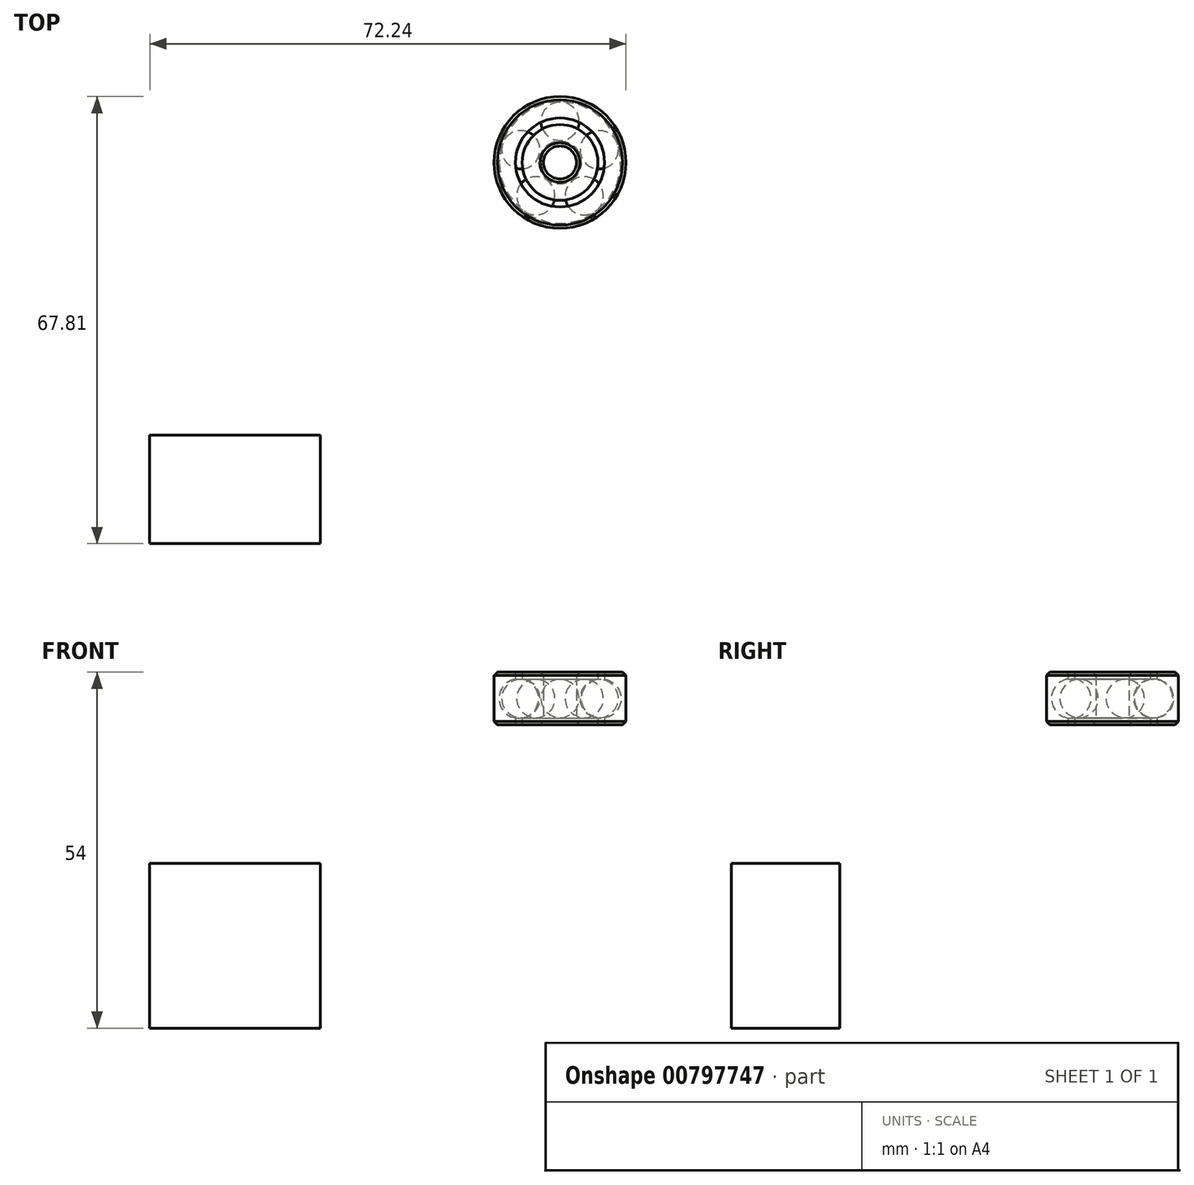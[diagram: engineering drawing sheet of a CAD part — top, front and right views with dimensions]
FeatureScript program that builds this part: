
annotation { "Feature Type Name" : "Feature", "Feature Type Description" : "" }
export const myFeature = defineFeature(function(context is Context, id is Id, definition is map)
    precondition{}
    {
        {
            assignVariable(context, id + "F0", {"name" : "espacio_alto", "anyValue" : 50});
        }
        {
            assignVariable(context, id + "F1", {"name" : "espacio_atras", "anyValue" : 0});
        }
        {
            assignVariable(context, id + "F2", {"name" : "espacio_lateral", "anyValue" : 0});
        }
        {
            var Q0;
            Q0=qCreatedBy(makeId("Right.planeOp"),FACE);
            var sketch = newSketch(context, id + "F3", { "sketchPlane" : qUnion([Q0])});
            skLineSegment(sketch, "E0", {"start": v(0, 0) * mm, "end": v(0, 7.32) * mm, "construction": true});
            skArc(sketch, "E1", {"start": v(6.25, 3) * mm, "mid": v(9.25, 0) * mm, "end": v(6.25, -3) * mm});
            skLineSegment(sketch, "E2", {"start": v(6.25, 3) * mm, "end": v(6.25, -3) * mm});
            skLineSegment(sketch, "E3", {"start": v(6.75, 2.96) * mm, "end": v(6.75, -2.96) * mm});
            skLineSegment(sketch, "E4", {"start": v(6.25, 3) * mm, "end": v(6.25, 4) * mm});
            skLineSegment(sketch, "E5", {"start": v(6.25, 4) * mm, "end": v(10, 4) * mm});
            skLineSegment(sketch, "E6", {"start": v(10, 4) * mm, "end": v(10, 0) * mm});
            skLineSegment(sketch, "E7", {"start": v(0, 0) * mm, "end": v(-2.34, 0) * mm, "construction": true});
            skLineSegment(sketch, "E8.MirrorCS", {"start": v(6.25, -4) * mm, "end": v(10, -4) * mm});
            skLineSegment(sketch, "E9.MirrorCS", {"start": v(10, -4) * mm, "end": v(10, 0) * mm});
            skLineSegment(sketch, "E10.MirrorCS", {"start": v(6.25, -3) * mm, "end": v(6.25, -4) * mm});
            skLineSegment(sketch, "E11.MirrorCS", {"start": v(6.25, 4) * mm, "end": v(2.5, 4) * mm});
            skLineSegment(sketch, "E12.MirrorCS", {"start": v(2.5, 4) * mm, "end": v(2.5, 0) * mm});
            skLineSegment(sketch, "E13.MirrorCS", {"start": v(5.75, 2.96) * mm, "end": v(5.75, -2.96) * mm});
            skArc(sketch, "E14.MirrorCS", {"start": v(6.25, 3) * mm, "mid": v(3.25, 0) * mm, "end": v(6.25, -3) * mm});
            skLineSegment(sketch, "E15.MirrorCS", {"start": v(6.25, -4) * mm, "end": v(2.5, -4) * mm});
            skLineSegment(sketch, "E16.MirrorCS", {"start": v(2.5, -4) * mm, "end": v(2.5, 0) * mm});
            skLineSegment(sketch, "E17", {"start": v(5.75, -4) * mm, "end": v(5.75, 4) * mm});
            skLineSegment(sketch, "E18", {"start": v(6.75, -4) * mm, "end": v(6.75, 4) * mm});
            skSolve(sketch);
        }
        {
            var Q0;
            Q0=qCreatedBy(makeId("Right.planeOp"),FACE);
            var sketch = newSketch(context, id + "F4", { "sketchPlane" : qUnion([Q0])});
            skArc(sketch, "E19.0", {"start": v(6.25, 2.9) * mm, "mid": v(3.35, 0) * mm, "end": v(6.25, -2.9) * mm});
            skLineSegment(sketch, "E20", {"start": v(6.25, 2.9) * mm, "end": v(6.25, -2.9) * mm});
            skSolve(sketch);
        }
        {
            var Q0;
            Q0=makeQuery(id+"F4.imprint","IMPRINT",FACE,{"disambiguationData":[TD([[makeQuery(id+"F4.imprint","IMPRINT",EDGE,{"derivedFrom":sQuery(id+"F4.wireOp",EDGE,"E19.0")}),1.0]])]});
            var Q1;
            Q1=sQuery(id+"F4.wireOp",EDGE,"E20");
            revolve(context, id + "F5", {"surfaceOperationType" : NewSurfaceOperationType.NEW, "entities" : qUnion([Q0]), "axis" : qUnion([Q1]), "revolveType" : RevolveType.FULL});
        }
        {
            var Q0;
            {var subQ7=sQuery(id+"F3.wireOp",EDGE,"E12.MirrorCS");Q0=makeQuery(id+"F3.imprint","IMPRINT",FACE,{"disambiguationData":[TD([[makeQuery(id+"F3.imprint","IMPRINT",EDGE,{"derivedFrom":subQ7}),1.0]])]});}
            var Q1;
            {var subQ4=sQuery(id+"F3.wireOp",EDGE,"E6");Q1=makeQuery(id+"F3.imprint","IMPRINT",FACE,{"disambiguationData":[TD([[makeQuery(id+"F3.imprint","IMPRINT",EDGE,{"derivedFrom":subQ4}),-1.0]])]});}
            var Q2;
            Q2=sQuery(id+"F3.wireOp",EDGE,"E0");
            revolve(context, id + "F6", {"surfaceOperationType" : NewSurfaceOperationType.NEW, "entities" : qUnion([Q0, Q1]), "axis" : qUnion([Q2]), "revolveType" : RevolveType.FULL});
        }
        {
            var Q0;
            Q0=makeQuery(id+"F6.opRevolve","SWEPT_EDGE",EDGE,{"disambiguationData":[OSD([sQuery(id+"F3.wireOp",EDGE,"E5"),sQuery(id+"F3.wireOp",EDGE,"E6")])]});
            var Q1;
            Q1=makeQuery(id+"F6.opRevolve","SWEPT_EDGE",EDGE,{"disambiguationData":[OSD([sQuery(id+"F3.wireOp",EDGE,"E8.MirrorCS"),sQuery(id+"F3.wireOp",EDGE,"E9.MirrorCS")])]});
            var Q2;
            Q2=makeQuery(id+"F6.opRevolve","SWEPT_EDGE",EDGE,{"disambiguationData":[OSD([sQuery(id+"F3.wireOp",EDGE,"E11.MirrorCS"),sQuery(id+"F3.wireOp",EDGE,"E12.MirrorCS")])]});
            var Q3;
            Q3=makeQuery(id+"F6.opRevolve","SWEPT_EDGE",EDGE,{"disambiguationData":[OSD([sQuery(id+"F3.wireOp",EDGE,"E15.MirrorCS"),sQuery(id+"F3.wireOp",EDGE,"E16.MirrorCS")])]});
            chamfer(context, id + "F7", {"entities" : qUnion([Q0, Q1, Q2, Q3]), "width" : 0.5 * mm, "tangentPropagation" : true});
        }
        {
            var Q0;
            Q0=makeQuery(id+"F5.opRevolve","SWEPT_BODY",BODY,{"disambiguationData":[OSD([sQuery(id+"F4.wireOp",EDGE,"E19.0"),sQuery(id+"F4.wireOp",EDGE,"E20")])]});
            var Q1;
            Q1=sQuery(id+"F3.wireOp",EDGE,"E0");
            circularPattern(context, id + "F8", {"entities" : qUnion([Q0]), "axis" : qUnion([Q1]), "angle" : 360 * degree, "instanceCount" : 5, "equalSpace" : true});
        }
        {
            var Q0;
            Q0=makeQuery(id+"F6.opRevolve","SWEPT_BODY",BODY,{"disambiguationData":[OSD([sQuery(id+"F3.wireOp",EDGE,"E11.MirrorCS"),sQuery(id+"F3.wireOp",EDGE,"E12.MirrorCS"),sQuery(id+"F3.wireOp",EDGE,"E14.MirrorCS"),sQuery(id+"F3.wireOp",EDGE,"E15.MirrorCS"),sQuery(id+"F3.wireOp",EDGE,"E16.MirrorCS"),sQuery(id+"F3.wireOp",EDGE,"E17")])]});
            var Q1;
            Q1=makeQuery(id+"F8.opPattern","COPY",BODY,{"derivedFrom":makeQuery(id+"F5.opRevolve","SWEPT_BODY",BODY,{"disambiguationData":[OSD([sQuery(id+"F4.wireOp",EDGE,"E19.0"),sQuery(id+"F4.wireOp",EDGE,"E20")])]}),"instanceName":"8"});
            var Q2;
            Q2=makeQuery(id+"F6.opRevolve","SWEPT_BODY",BODY,{"disambiguationData":[OSD([sQuery(id+"F3.wireOp",EDGE,"E1"),sQuery(id+"F3.wireOp",EDGE,"E5"),sQuery(id+"F3.wireOp",EDGE,"E6"),sQuery(id+"F3.wireOp",EDGE,"E8.MirrorCS"),sQuery(id+"F3.wireOp",EDGE,"E9.MirrorCS"),sQuery(id+"F3.wireOp",EDGE,"E18")])]});
            var Q3;
            Q3=makeQuery(id+"F8.opPattern","COPY",BODY,{"derivedFrom":makeQuery(id+"F5.opRevolve","SWEPT_BODY",BODY,{"disambiguationData":[OSD([sQuery(id+"F4.wireOp",EDGE,"E19.0"),sQuery(id+"F4.wireOp",EDGE,"E20")])]}),"instanceName":"3"});
            var Q4;
            Q4=makeQuery(id+"F8.opPattern","COPY",BODY,{"derivedFrom":makeQuery(id+"F5.opRevolve","SWEPT_BODY",BODY,{"disambiguationData":[OSD([sQuery(id+"F4.wireOp",EDGE,"E19.0"),sQuery(id+"F4.wireOp",EDGE,"E20")])]}),"instanceName":"5"});
            var Q5;
            Q5=makeQuery(id+"F8.opPattern","COPY",BODY,{"derivedFrom":makeQuery(id+"F5.opRevolve","SWEPT_BODY",BODY,{"disambiguationData":[OSD([sQuery(id+"F4.wireOp",EDGE,"E19.0"),sQuery(id+"F4.wireOp",EDGE,"E20")])]}),"instanceName":"11"});
            var Q6;
            Q6=makeQuery(id+"F8.opPattern","COPY",BODY,{"derivedFrom":makeQuery(id+"F5.opRevolve","SWEPT_BODY",BODY,{"disambiguationData":[OSD([sQuery(id+"F4.wireOp",EDGE,"E19.0"),sQuery(id+"F4.wireOp",EDGE,"E20")])]}),"instanceName":"6"});
            var Q7;
            Q7=makeQuery(id+"F8.opPattern","COPY",BODY,{"derivedFrom":makeQuery(id+"F5.opRevolve","SWEPT_BODY",BODY,{"disambiguationData":[OSD([sQuery(id+"F4.wireOp",EDGE,"E19.0"),sQuery(id+"F4.wireOp",EDGE,"E20")])]}),"instanceName":"9"});
            var Q8;
            Q8=makeQuery(id+"F8.opPattern","COPY",BODY,{"derivedFrom":makeQuery(id+"F5.opRevolve","SWEPT_BODY",BODY,{"disambiguationData":[OSD([sQuery(id+"F4.wireOp",EDGE,"E19.0"),sQuery(id+"F4.wireOp",EDGE,"E20")])]}),"instanceName":"1"});
            var Q9;
            Q9=makeQuery(id+"F8.opPattern","COPY",BODY,{"derivedFrom":makeQuery(id+"F5.opRevolve","SWEPT_BODY",BODY,{"disambiguationData":[OSD([sQuery(id+"F4.wireOp",EDGE,"E19.0"),sQuery(id+"F4.wireOp",EDGE,"E20")])]}),"instanceName":"7"});
            var Q10;
            Q10=makeQuery(id+"F8.opPattern","COPY",BODY,{"derivedFrom":makeQuery(id+"F5.opRevolve","SWEPT_BODY",BODY,{"disambiguationData":[OSD([sQuery(id+"F4.wireOp",EDGE,"E19.0"),sQuery(id+"F4.wireOp",EDGE,"E20")])]}),"instanceName":"2"});
            var Q11;
            Q11=makeQuery(id+"F8.opPattern","COPY",BODY,{"derivedFrom":makeQuery(id+"F5.opRevolve","SWEPT_BODY",BODY,{"disambiguationData":[OSD([sQuery(id+"F4.wireOp",EDGE,"E19.0"),sQuery(id+"F4.wireOp",EDGE,"E20")])]}),"instanceName":"4"});
            var Q12;
            Q12=makeQuery(id+"F8.opPattern","COPY",BODY,{"derivedFrom":makeQuery(id+"F5.opRevolve","SWEPT_BODY",BODY,{"disambiguationData":[OSD([sQuery(id+"F4.wireOp",EDGE,"E19.0"),sQuery(id+"F4.wireOp",EDGE,"E20")])]}),"instanceName":"10"});
            var Q13;
            Q13=makeQuery(id+"F5.opRevolve","SWEPT_BODY",BODY,{"disambiguationData":[OSD([sQuery(id+"F4.wireOp",EDGE,"E19.0"),sQuery(id+"F4.wireOp",EDGE,"E20")])]});
            transform(context, id + "F9", {"entities" : qUnion([Q0, Q1, Q2, Q3, Q4, Q5, Q6, Q7, Q8, Q9, Q10, Q11, Q12, Q13]), "transformType" : TransformType.TRANSLATION_3D, "dx" : (getVariable(context, 'espacio_lateral')) * mm, "dy" : (getVariable(context, 'espacio_atras')) * mm, "dz" : (getVariable(context, 'espacio_alto')) * mm, "makeCopy" : false});
        }
        {
            var Q0;
            Q0=qCreatedBy(makeId("Top.planeOp"),FACE);
            var sketch = newSketch(context, id + "F10", { "sketchPlane" : qUnion([Q0])});
            skLineSegment(sketch, "E21.bottom", {"start": v(-62.24, -57.81) * mm, "end": v(-36.35, -57.81) * mm});
            skLineSegment(sketch, "E21.top", {"start": v(-62.24, -41.37) * mm, "end": v(-36.35, -41.37) * mm});
            skLineSegment(sketch, "E21.left", {"start": v(-62.24, -57.81) * mm, "end": v(-62.24, -41.37) * mm});
            skLineSegment(sketch, "E21.right", {"start": v(-36.35, -57.81) * mm, "end": v(-36.35, -41.37) * mm});
            skSolve(sketch);
        }
        {
            var Q0;
            Q0 = qSketchRegion(id + "F10", true);
            extrude(context, id + "F11", {"entities" : qUnion([Q0]), "depth" : 25 * mm, "offsetDistance" : 25 * mm});
        }
    });
